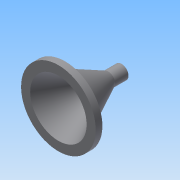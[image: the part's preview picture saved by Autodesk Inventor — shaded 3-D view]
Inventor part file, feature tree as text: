
AUTODESK INVENTOR PART (.ipt)
format: ipt  version: 2015 SP1 (Build 190203100, 203)  size: 95,232 bytes
history: native  units: mm
features: revolve x1, sketch x1
ambient origin geometry x8: Origin, YZ Plane, XZ Plane, XY Plane, X Axis, Y Axis, Z Axis, Center Point
bodies: Solid1 (feature_tree)
feature tree (2):
  revolve  "Revolution1"  [1 undecoded]
  sketch  "Sketch1"  dims[d0=17.78mm d1=3.175mm d2=4.318mm d3=30.099mm d4=90.0deg]
note: 1 required parameter value undecoded (feature->parameter linkage not recoverable at this tier; creation-order binding heuristic only, values carry confidence <= 0.55)
